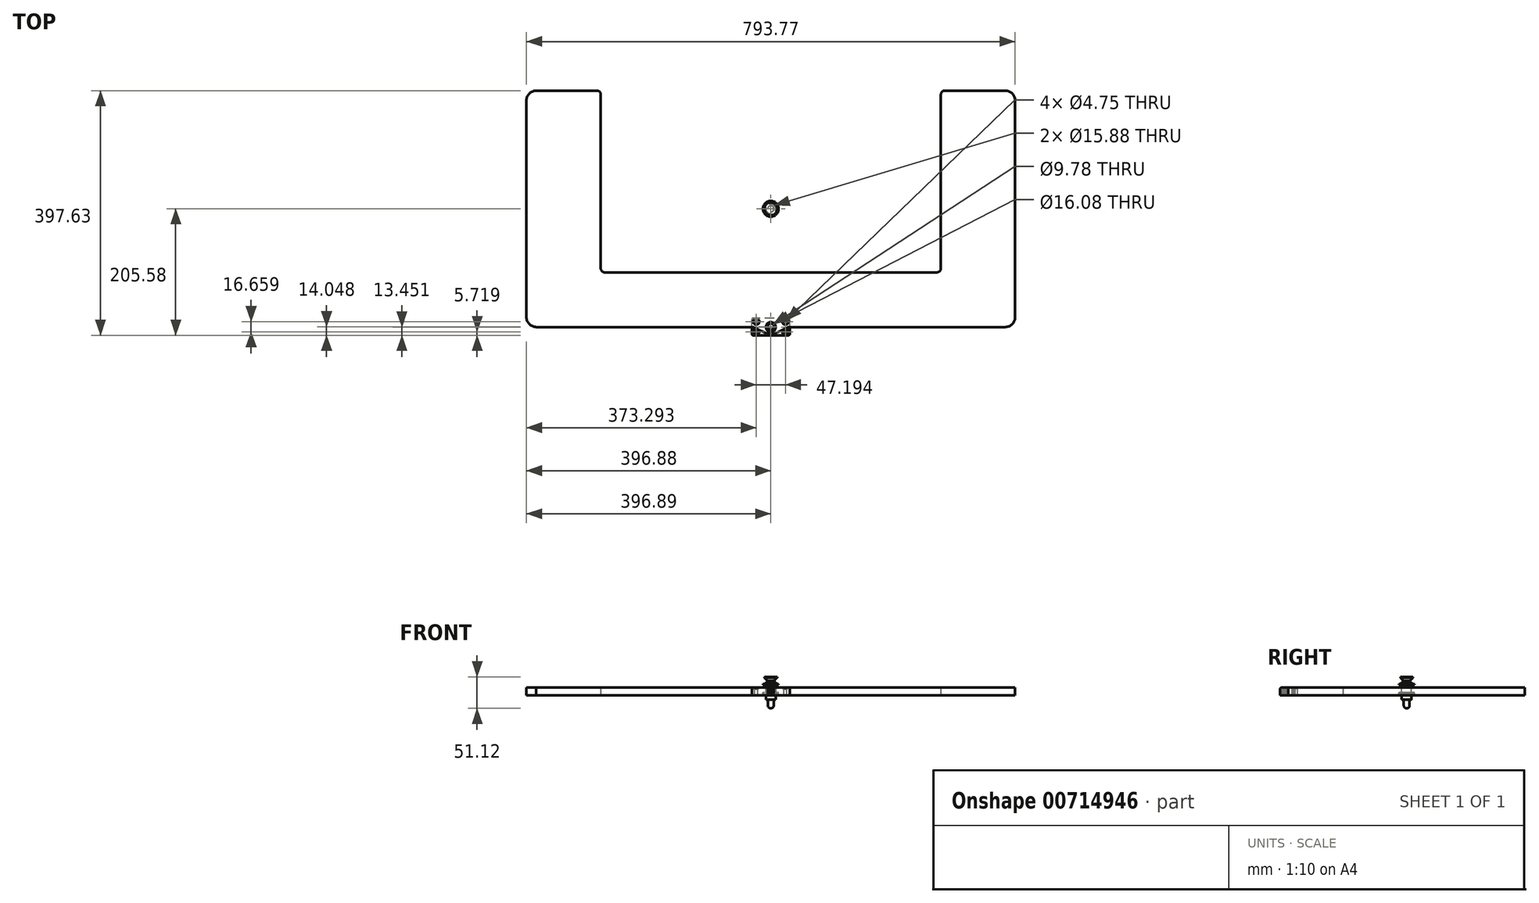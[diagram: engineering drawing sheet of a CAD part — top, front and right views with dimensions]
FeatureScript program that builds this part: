
annotation { "Feature Type Name" : "Feature", "Feature Type Description" : "" }
export const myFeature = defineFeature(function(context is Context, id is Id, definition is map)
    precondition{}
    {
        {
            var Q0;
            Q0=qCreatedBy(makeId("Top.planeOp"),FACE);
            var sketch = newSketch(context, id + "F0", { "sketchPlane" : qUnion([Q0])});
            skLineSegment(sketch, "E0.bottom", {"start": v(-381.02, -192.13) * mm, "end": v(-29.92, -192.13) * mm});
            skLineSegment(sketch, "E0.top", {"start": v(-381.02, 192.05) * mm, "end": v(-282.6, 192.05) * mm});
            skLineSegment(sketch, "E0.right", {"start": v(396.88, -176.25) * mm, "end": v(396.88, 176.17) * mm});
            skLineSegment(sketch, "E1.trimOffspring", {"start": v(-396.9, -176.06) * mm, "end": v(-396.9, 176.17) * mm});
            skPoint(sketch, "E2.visualSharp", {"position": v(-396.9, -192.13) * mm});
            skPoint(sketch, "E3.visualSharp", {"position": v(-396.9, 192.05) * mm});
            skLineSegment(sketch, "E4.top", {"start": v(-269.9, -103.23) * mm, "end": v(269.88, -103.23) * mm});
            skLineSegment(sketch, "E4.left", {"start": v(-276.24, 185.7) * mm, "end": v(-276.24, -96.88) * mm});
            skLineSegment(sketch, "E4.right", {"start": v(276.23, 185.7) * mm, "end": v(276.23, -96.88) * mm});
            skLineSegment(sketch, "E5.trimOffspring", {"start": v(282.58, 192.05) * mm, "end": v(381, 192.05) * mm});
            skArc(sketch, "E6", {"start": v(-5.7, -203.5) * mm, "mid": v(0, -204.85) * mm, "end": v(5.69, -203.5) * mm});
            skLineSegment(sketch, "E7.trimOffspring", {"start": v(29.9, -192.13) * mm, "end": v(381, -192.13) * mm});
            skCircle(sketch, "E8", {"center": v(0, -192.13) * mm, "radius": 8.04 * mm});
            skLineSegment(sketch, "E9", {"start": v(5.69, -203.5) * mm, "end": v(27.06, -192.8) * mm});
            skLineSegment(sketch, "E10", {"start": v(-5.7, -203.5) * mm, "end": v(-27.07, -192.8) * mm});
            skPoint(sketch, "E11.visualSharp", {"position": v(-28.42, -192.13) * mm});
            skArc(sketch, "E11.filletArc", {"start": v(-27.07, -192.8) * mm, "mid": v(-28.46, -192.3) * mm, "end": v(-29.92, -192.13) * mm});
            skPoint(sketch, "E12.visualSharp", {"position": v(28.4, -192.13) * mm});
            skArc(sketch, "E12.filletArc", {"start": v(29.9, -192.13) * mm, "mid": v(28.44, -192.3) * mm, "end": v(27.06, -192.8) * mm});
            skArc(sketch, "E13", {"start": v(-381.02, 192.05) * mm, "mid": v(-392.24, 187.4) * mm, "end": v(-396.9, 176.17) * mm});
            skArc(sketch, "E14", {"start": v(-396.9, -176.06) * mm, "mid": v(-392.26, -187.36) * mm, "end": v(-381.02, -192.13) * mm});
            skArc(sketch, "E15", {"start": v(381, -192.13) * mm, "mid": v(392.23, -187.48) * mm, "end": v(396.88, -176.25) * mm});
            skArc(sketch, "E16", {"start": v(396.88, 176.17) * mm, "mid": v(392.23, 187.4) * mm, "end": v(381, 192.05) * mm});
            skArc(sketch, "E17", {"start": v(282.58, 192.05) * mm, "mid": v(278.08, 190.19) * mm, "end": v(276.23, 185.7) * mm});
            skArc(sketch, "E18", {"start": v(276.23, -96.88) * mm, "mid": v(274.37, -101.37) * mm, "end": v(269.88, -103.23) * mm});
            skArc(sketch, "E19", {"start": v(-269.9, -103.23) * mm, "mid": v(-274.38, -101.37) * mm, "end": v(-276.24, -96.88) * mm});
            skArc(sketch, "E20", {"start": v(-276.24, 185.7) * mm, "mid": v(-278.1, 190.19) * mm, "end": v(-282.6, 192.05) * mm});
            skSolve(sketch);
        }
        {
            var Q0;
            Q0=makeQuery(id+"F0.imprint","IMPRINT",FACE,{"disambiguationData":[TD([[makeQuery(id+"F0.imprint","IMPRINT",EDGE,{"derivedFrom":sQuery(id+"F0.wireOp",EDGE,"E0.bottom")}),1.0]])]});
            extrude(context, id + "F1", {"entities" : qUnion([Q0]), "depth" : 12.7 * mm, "offsetDistance" : 25.4 * mm});
        }
        {
            var Q0;
            Q0=qCreatedBy(makeId("Top.planeOp"),FACE);
            var sketch = newSketch(context, id + "F2", { "sketchPlane" : qUnion([Q0])});
            skLineSegment(sketch, "E21.bottom", {"start": v(31, -205.58) * mm, "end": v(-31, -205.58) * mm});
            skLineSegment(sketch, "E21.top", {"start": v(31, -177.48) * mm, "end": v(-31, -177.48) * mm});
            skLineSegment(sketch, "E21.left", {"start": v(31, -205.58) * mm, "end": v(31, -177.48) * mm});
            skLineSegment(sketch, "E21.right", {"start": v(-31, -205.58) * mm, "end": v(-31, -177.48) * mm});
            skPoint(sketch, "E21.middle", {"position": v(0, -191.53) * mm});
            skCircle(sketch, "E22", {"center": v(0, -191.53) * mm, "radius": 4.89 * mm});
            skSolve(sketch);
        }
        {
            var Q0;
            Q0 = qSketchRegion(id + "F2", true);
            extrude(context, id + "F3", {"entities" : qUnion([Q0]), "depth" : 12.7 * mm, "offsetDistance" : 25.4 * mm});
        }
        {
            var Q0;
            Q0=qCreatedBy(makeId("Right.planeOp"),FACE);
            var sketch = newSketch(context, id + "F4", { "sketchPlane" : qUnion([Q0])});
            skLineSegment(sketch, "E23", {"start": v(-205.58, 2.05) * mm, "end": v(-192.89, 12.7) * mm});
            skSolve(sketch);
        }
        {
            var Q0;
            Q0=makeQuery(id+"F3.opExtrude","SWEPT_FACE",FACE,{"disambiguationData":[OSD([sQuery(id+"F2.wireOp",EDGE,"E21.bottom")])]});
            var sketch = newSketch(context, id + "F5", { "sketchPlane" : qUnion([Q0])});
            skArc(sketch, "E24", {"start": v(-4.76, 5.36) * mm, "mid": v(0, 0.6) * mm, "end": v(4.76, 5.36) * mm});
            skLineSegment(sketch, "E25", {"start": v(-4.76, 5.36) * mm, "end": v(-4.76, 12.7) * mm});
            skLineSegment(sketch, "E26", {"start": v(-4.76, 12.7) * mm, "end": v(4.76, 12.7) * mm});
            skLineSegment(sketch, "E27", {"start": v(4.76, 12.7) * mm, "end": v(4.76, 5.36) * mm});
            skSolve(sketch);
        }
        {
            var Q0;
            Q0=makeQuery(id+"F5.imprint","IMPRINT",FACE,{"disambiguationData":[TD([[makeQuery(id+"F5.imprint","IMPRINT",EDGE,{"derivedFrom":sQuery(id+"F5.wireOp",EDGE,"E24")}),1.0]])]});
            var Q1;
            Q1=sQuery(id+"F4.wireOp",EDGE,"E23");
            sweep(context, id + "F6", {"operationType" : NewBodyOperationType.REMOVE, "profiles" : qUnion([Q0]), "path" : qUnion([Q1])});
        }
        {
            var Q0;
            Q0=makeQuery(id+"F3.opExtrude","CAP_EDGE",EDGE,{"disambiguationData":[OSD([sQuery(id+"F2.wireOp",EDGE,"E21.right")])],"isStart":false});
            var Q1;
            {var subQ0=sQuery(id+"F2.wireOp",EDGE,"E21.bottom");var subQ1=sQuery(id+"F2.wireOp",EDGE,"E21.right");Q1=makeQuery(id+"F6.boolean.opBoolean","SPLIT",EDGE,{"disambiguationData":[TD([makeQuery(id+"F3.opExtrude","SWEPT_FACE",FACE,{"disambiguationData":[OSD([subQ1])]})])],"derivedFrom":makeQuery(id+"F3.opExtrude","CAP_EDGE",EDGE,{"disambiguationData":[OSD([subQ0])],"isStart":false})});}
            var Q2;
            {var subQ0=sQuery(id+"F2.wireOp",EDGE,"E21.bottom");var subQ1=sQuery(id+"F2.wireOp",EDGE,"E21.left");Q2=makeQuery(id+"F6.boolean.opBoolean","SPLIT",EDGE,{"disambiguationData":[TD([makeQuery(id+"F3.opExtrude","SWEPT_FACE",FACE,{"disambiguationData":[OSD([subQ1])]})])],"derivedFrom":makeQuery(id+"F3.opExtrude","CAP_EDGE",EDGE,{"disambiguationData":[OSD([subQ0])],"isStart":false})});}
            var Q3;
            Q3=makeQuery(id+"F3.opExtrude","CAP_EDGE",EDGE,{"disambiguationData":[OSD([sQuery(id+"F2.wireOp",EDGE,"E21.left")])],"isStart":false});
            var Q4;
            Q4=makeQuery(id+"F3.opExtrude","CAP_EDGE",EDGE,{"disambiguationData":[OSD([sQuery(id+"F2.wireOp",EDGE,"E21.top")])],"isStart":false});
            var Q5;
            Q5=makeQuery(id+"F3.opExtrude","SWEPT_EDGE",EDGE,{"disambiguationData":[OSD([sQuery(id+"F2.wireOp",EDGE,"E21.bottom"),sQuery(id+"F2.wireOp",EDGE,"E21.left")])]});
            var Q6;
            Q6=makeQuery(id+"F3.opExtrude","SWEPT_EDGE",EDGE,{"disambiguationData":[OSD([sQuery(id+"F2.wireOp",EDGE,"E21.top"),sQuery(id+"F2.wireOp",EDGE,"E21.left")])]});
            var Q7;
            Q7=makeQuery(id+"F3.opExtrude","SWEPT_EDGE",EDGE,{"disambiguationData":[OSD([sQuery(id+"F2.wireOp",EDGE,"E21.bottom"),sQuery(id+"F2.wireOp",EDGE,"E21.right")])]});
            var Q8;
            Q8=makeQuery(id+"F3.opExtrude","SWEPT_EDGE",EDGE,{"disambiguationData":[OSD([sQuery(id+"F2.wireOp",EDGE,"E21.top"),sQuery(id+"F2.wireOp",EDGE,"E21.right")])]});
            fillet(context, id + "F7", {"entities" : qUnion([Q0, Q1, Q2, Q3, Q4, Q5, Q6, Q7, Q8]), "radius" : 2.54 * mm, "tangentPropagation" : true, "allowEdgeOverflow" : false});
        }
        {
            var Q0;
            Q0=makeQuery(id+"F3.opExtrude","CAP_FACE",FACE,{"disambiguationData":[OSD([sQuery(id+"F2.wireOp",EDGE,"E21.bottom"),sQuery(id+"F2.wireOp",EDGE,"E21.top"),sQuery(id+"F2.wireOp",EDGE,"E21.left"),sQuery(id+"F2.wireOp",EDGE,"E21.right"),sQuery(id+"F2.wireOp",EDGE,"E22")])],"isStart":false});
            var sketch = newSketch(context, id + "F8", { "sketchPlane" : qUnion([Q0])});
            skLineSegment(sketch, "E28.bottom", {"start": v(23.6, -199.86) * mm, "end": v(-23.6, -199.86) * mm, "construction": true});
            skLineSegment(sketch, "E28.top", {"start": v(23.6, -183.2) * mm, "end": v(-23.6, -183.2) * mm, "construction": true});
            skLineSegment(sketch, "E28.left", {"start": v(23.6, -199.86) * mm, "end": v(23.6, -183.2) * mm, "construction": true});
            skLineSegment(sketch, "E28.right", {"start": v(-23.6, -199.86) * mm, "end": v(-23.6, -183.2) * mm, "construction": true});
            skPoint(sketch, "E28.middle", {"position": v(0, -191.53) * mm});
            skPoint(sketch, "E29", {"position": v(-23.6, -183.2) * mm});
            skPoint(sketch, "E30", {"position": v(-23.6, -199.86) * mm});
            skPoint(sketch, "E31", {"position": v(23.6, -199.86) * mm});
            skPoint(sketch, "E32", {"position": v(23.6, -183.2) * mm});
            skSolve(sketch);
        }
        {
            var Q0;
            Q0=sQuery(id+"F8.wireOp",VERTEX,"E29");
            var Q1;
            Q1=sQuery(id+"F8.wireOp",VERTEX,"E32");
            var Q2;
            Q2=sQuery(id+"F8.wireOp",VERTEX,"E31");
            var Q3;
            Q3=sQuery(id+"F8.wireOp",VERTEX,"E30");
            var Q4;
            Q4=makeQuery(id+"F3.opExtrude","SWEPT_BODY",BODY,{"disambiguationData":[OSD([sQuery(id+"F2.wireOp",EDGE,"E21.bottom"),sQuery(id+"F2.wireOp",EDGE,"E21.top"),sQuery(id+"F2.wireOp",EDGE,"E21.left"),sQuery(id+"F2.wireOp",EDGE,"E21.right"),sQuery(id+"F2.wireOp",EDGE,"E22")])]});
            hole(context, id + "F9", {"style" : HoleStyle.C_SINK, "endStyle" : HoleEndStyle.THROUGH, "holeDiameter" : 4.75 * mm, "cSinkDiameter" : 10.16 * mm, "cSinkAngle" : 82 * degree, "majorDiameter" : 6.35 * mm, "tappedDepth" : 12.7 * mm, "tapClearance" : 3, "startFromSketch" : true, "locations" : qUnion([Q0, Q1, Q2, Q3]), "scope" : qUnion([Q4])});
        }
        {
            var Q0;
            Q0=qCreatedBy(makeId("Front.planeOp"),FACE);
            var sketch = newSketch(context, id + "F10", { "sketchPlane" : qUnion([Q0])});
            skLineSegment(sketch, "E33", {"start": v(4.76, -16.25) * mm, "end": v(4.76, -6.8) * mm});
            skLineSegment(sketch, "E34", {"start": v(4.76, -6.8) * mm, "end": v(7.94, -6.8) * mm});
            skLineSegment(sketch, "E35", {"start": v(7.94, -6.8) * mm, "end": v(7.94, 21.79) * mm});
            skLineSegment(sketch, "E36", {"start": v(7.94, 21.79) * mm, "end": v(5.08, 21.79) * mm});
            skLineSegment(sketch, "E37", {"start": v(5.08, 21.79) * mm, "end": v(5.08, 23.75) * mm});
            skLineSegment(sketch, "E38", {"start": v(5.08, 23.75) * mm, "end": v(10.41, 28.6) * mm});
            skLineSegment(sketch, "E39", {"start": v(10.41, 30.1) * mm, "end": v(0, 30.1) * mm});
            skLineSegment(sketch, "E40", {"start": v(0, 30.1) * mm, "end": v(0, -21.02) * mm});
            skArc(sketch, "E41", {"start": v(0, -21.02) * mm, "mid": v(3.37, -19.62) * mm, "end": v(4.76, -16.25) * mm});
            skLineSegment(sketch, "E42", {"start": v(10.41, 30.1) * mm, "end": v(10.41, 28.6) * mm});
            skPoint(sketch, "E43.orphan", {"position": v(7.94, 26.35) * mm});
            skLineSegment(sketch, "E44.bottom", {"start": v(7.94, 18.61) * mm, "end": v(12.69, 18.61) * mm});
            skLineSegment(sketch, "E44.top", {"start": v(7.94, 17.01) * mm, "end": v(12.69, 17.01) * mm});
            skLineSegment(sketch, "E44.left", {"start": v(7.94, 18.61) * mm, "end": v(7.94, 17.01) * mm});
            skLineSegment(sketch, "E44.right", {"start": v(12.69, 18.61) * mm, "end": v(12.69, 17.01) * mm});
            skLineSegment(sketch, "E45.bottom", {"start": v(7.94, 2.71) * mm, "end": v(12.69, 2.71) * mm});
            skLineSegment(sketch, "E45.top", {"start": v(7.94, 4.31) * mm, "end": v(12.69, 4.31) * mm});
            skLineSegment(sketch, "E45.left", {"start": v(7.94, 2.71) * mm, "end": v(7.94, 4.31) * mm});
            skLineSegment(sketch, "E45.right", {"start": v(12.69, 2.71) * mm, "end": v(12.69, 4.31) * mm});
            skSolve(sketch);
        }
        {
            var Q0;
            Q0=makeQuery(id+"F10.imprint","IMPRINT",FACE,{"disambiguationData":[TD([[makeQuery(id+"F10.imprint","IMPRINT",EDGE,{"derivedFrom":sQuery(id+"F10.wireOp",EDGE,"E33")}),1.0]])]});
            var Q1;
            Q1=sQuery(id+"F10.wireOp",EDGE,"E40");
            revolve(context, id + "F11", {"surfaceOperationType" : NewSurfaceOperationType.NEW, "entities" : qUnion([Q0]), "axis" : qUnion([Q1]), "revolveType" : RevolveType.FULL});
        }
        {
            var Q0;
            Q0=makeQuery(id+"F10.imprint","IMPRINT",FACE,{"disambiguationData":[TD([[makeQuery(id+"F10.imprint","IMPRINT",EDGE,{"derivedFrom":sQuery(id+"F10.wireOp",EDGE,"E44.bottom")}),-1.0]])]});
            var Q1;
            Q1=makeQuery(id+"F10.imprint","IMPRINT",FACE,{"disambiguationData":[TD([[makeQuery(id+"F10.imprint","IMPRINT",EDGE,{"derivedFrom":sQuery(id+"F10.wireOp",EDGE,"E45.bottom")}),1.0]])]});
            var Q2;
            Q2=sQuery(id+"F10.wireOp",EDGE,"E40");
            revolve(context, id + "F12", {"surfaceOperationType" : NewSurfaceOperationType.NEW, "entities" : qUnion([Q0, Q1]), "axis" : qUnion([Q2]), "revolveType" : RevolveType.FULL});
        }
    });
